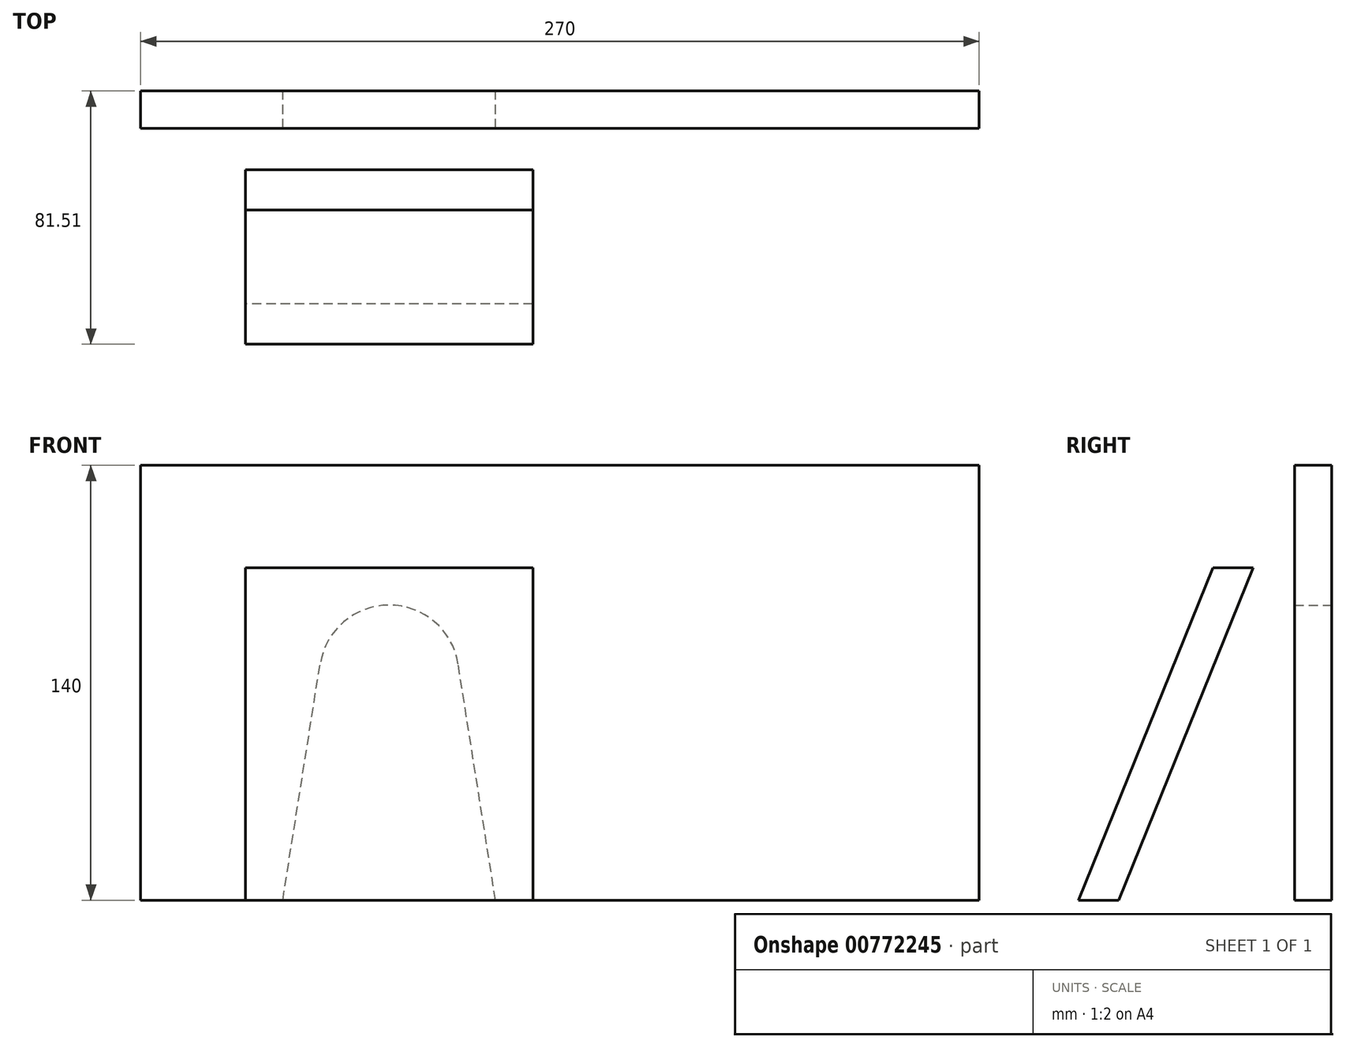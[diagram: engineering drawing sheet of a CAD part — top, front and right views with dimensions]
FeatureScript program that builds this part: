
annotation { "Feature Type Name" : "Feature", "Feature Type Description" : "" }
export const myFeature = defineFeature(function(context is Context, id is Id, definition is map)
    precondition{}
    {
        {
            var Q0;
            Q0=qCreatedBy(makeId("Front.planeOp"),FACE);
            var sketch = newSketch(context, id + "F0", { "sketchPlane" : qUnion([Q0])});
            skLineSegment(sketch, "E0.bottom", {"start": v(0, 0) * mm, "end": v(45.74, 0) * mm});
            skLineSegment(sketch, "E0.top", {"start": v(0, 140) * mm, "end": v(270, 140) * mm});
            skLineSegment(sketch, "E0.left", {"start": v(0, 0) * mm, "end": v(0, 140) * mm});
            skLineSegment(sketch, "E0.right", {"start": v(270, 0) * mm, "end": v(270, 140) * mm});
            skLineSegment(sketch, "E1", {"start": v(80, 140) * mm, "end": v(80, 0) * mm, "construction": true});
            skLineSegment(sketch, "E2", {"start": v(45.74, 0) * mm, "end": v(57.78, 76.02) * mm});
            skLineSegment(sketch, "E3", {"start": v(114.26, 0) * mm, "end": v(102.22, 76.02) * mm});
            skPoint(sketch, "E4", {"position": v(80, 95) * mm});
            skLineSegment(sketch, "E5", {"start": v(102.22, 76.02) * mm, "end": v(102.22, 76.02) * mm});
            skArc(sketch, "E6", {"start": v(102.22, 76.02) * mm, "mid": v(80, 95) * mm, "end": v(57.78, 76.02) * mm});
            skLineSegment(sketch, "E7.trimOffspring", {"start": v(114.26, 0) * mm, "end": v(270, 0) * mm});
            skSolve(sketch);
        }
        {
            var Q0;
            Q0=qSketchRegion(id+"F0",true);
            extrude(context, id + "F1", {"entities" : qUnion([Q0]), "depth" : 12 * mm, "offsetDistance" : 25 * mm});
        }
        {
            var Q0;
            Q0=makeQuery(id+"F1.opExtrude","CAP_FACE",FACE,{"disambiguationData":[OSD([sQuery(id+"F0.wireOp",EDGE,"E0.bottom"),sQuery(id+"F0.wireOp",EDGE,"E0.top"),sQuery(id+"F0.wireOp",EDGE,"E0.left"),sQuery(id+"F0.wireOp",EDGE,"E0.right"),sQuery(id+"F0.wireOp",EDGE,"E2"),sQuery(id+"F0.wireOp",EDGE,"E3"),sQuery(id+"F0.wireOp",EDGE,"E6"),sQuery(id+"F0.wireOp",EDGE,"E7.trimOffspring")])],"isStart":false});
            var sketch = newSketch(context, id + "F2", { "sketchPlane" : qUnion([Q0])});
            skLineSegment(sketch, "E8.0", {"start": v(114.26, 0) * mm, "end": v(114.26, 95) * mm});
            skLineSegment(sketch, "E9", {"start": v(114.26, 0) * mm, "end": v(126.26, 0) * mm});
            skLineSegment(sketch, "E10", {"start": v(126.26, 0) * mm, "end": v(126.26, 95) * mm});
            skLineSegment(sketch, "E11", {"start": v(126.26, 95) * mm, "end": v(114.26, 95) * mm});
            skLineSegment(sketch, "E12", {"start": v(33.74, 0) * mm, "end": v(33.74, 95) * mm});
            skLineSegment(sketch, "E13", {"start": v(33.74, 95) * mm, "end": v(45.74, 95) * mm});
            skLineSegment(sketch, "E14", {"start": v(33.74, 95) * mm, "end": v(126.26, 95) * mm});
            skPoint(sketch, "E14.startSnap0", {"position": v(80, 95) * mm});
            skLineSegment(sketch, "E15", {"start": v(33.74, 107) * mm, "end": v(126.26, 107) * mm});
            skLineSegment(sketch, "E16", {"start": v(33.74, 95) * mm, "end": v(33.74, 107) * mm});
            skLineSegment(sketch, "E17", {"start": v(126.26, 95) * mm, "end": v(126.26, 107) * mm});
            skLineSegment(sketch, "E18", {"start": v(45.74, 0) * mm, "end": v(33.74, 0) * mm});
            skLineSegment(sketch, "E19", {"start": v(45.74, 0) * mm, "end": v(45.74, 95) * mm});
            skSolve(sketch);
        }
        {
            var Q0;
            {var subQ3=sQuery(id+"F2.wireOp",EDGE,"E10");Q0=makeQuery(id+"F2.imprint","IMPRINT",FACE,{"disambiguationData":[TD([[makeQuery(id+"F2.imprint","IMPRINT",EDGE,{"derivedFrom":subQ3}),-1.0]])]});}
            var Q1;
            Q1=makeQuery(id+"F1.opExtrude","CAP_EDGE",EDGE,{"disambiguationData":[OSD([sQuery(id+"F0.wireOp",EDGE,"E0.top")])],"isStart":false});
            cPlane(context, id + "F3", {"entities" : qUnion([Q0, Q1]), "cplaneType" : CPlaneType.LINE_ANGLE, "offset" : 25 * mm, "angle" : 22 * degree, "oppositeDirection" : true, "width" : 150 * mm, "height" : 150 * mm});
        }
        {
            var Q0;
            Q0=qCreatedBy(id+"F3.planeOp",FACE);
            cPlane(context, id + "F4", {"entities" : qUnion([Q0]), "cplaneType" : CPlaneType.OFFSET, "offset" : 12 * mm, "oppositeDirection" : true, "width" : 150 * mm, "height" : 150 * mm});
        }
        {
            var Q0;
            {var subQ4=sQuery(id+"F2.wireOp",EDGE,"E12");Q0=makeQuery(id+"F2.imprint","IMPRINT",FACE,{"disambiguationData":[TD([[makeQuery(id+"F2.imprint","IMPRINT",EDGE,{"derivedFrom":subQ4}),-1.0]])]});}
            var Q1;
            Q1=qCreatedBy(id+"F3.planeOp",FACE);
            extrude(context, id + "F5", {"entities" : qUnion([Q0]), "endBound" : BoundingType.UP_TO_SURFACE, "depth" : 55 * mm, "endBoundEntityFace" : qUnion([Q1]), "offsetDistance" : 25 * mm});
        }
        {
            var Q0;
            {var subQ1=sQuery(id+"F2.wireOp",EDGE,"E9");Q0=makeQuery(id+"F2.imprint","IMPRINT",FACE,{"disambiguationData":[TD([[makeQuery(id+"F2.imprint","IMPRINT",EDGE,{"derivedFrom":subQ1}),1.0]])]});}
            var Q1;
            Q1=qCreatedBy(id+"F3.planeOp",FACE);
            extrude(context, id + "F6", {"entities" : qUnion([Q0]), "endBound" : BoundingType.UP_TO_SURFACE, "depth" : 55 * mm, "endBoundEntityFace" : qUnion([Q1]), "offsetDistance" : 25 * mm});
        }
        {
            var Q0;
            Q0=makeQuery(id+"F2.imprint","IMPRINT",FACE,{"disambiguationData":[TD([[makeQuery(id+"F2.imprint","IMPRINT",EDGE,{"derivedFrom":sQuery(id+"F2.wireOp",EDGE,"E15")}),-1.0]])]});
            var Q1;
            Q1=qCreatedBy(id+"F3.planeOp",FACE);
            extrude(context, id + "F7", {"entities" : qUnion([Q0]), "endBound" : BoundingType.UP_TO_SURFACE, "depth" : 55 * mm, "endBoundEntityFace" : qUnion([Q1]), "offsetDistance" : 25 * mm});
        }
        {
            var Q0;
            {var subQ3=sQuery(id+"F2.wireOp",EDGE,"E10");Q0=makeQuery(id+"F2.imprint","IMPRINT",FACE,{"disambiguationData":[TD([[makeQuery(id+"F2.imprint","IMPRINT",EDGE,{"derivedFrom":subQ3}),-1.0]])]});}
            var sketch = newSketch(context, id + "F8", { "sketchPlane" : qUnion([Q0])});
            skLineSegment(sketch, "E20.0", {"start": v(33.74, 0) * mm, "end": v(33.74, 95) * mm});
            skLineSegment(sketch, "E21.0", {"start": v(33.74, 95) * mm, "end": v(33.74, 107) * mm});
            skLineSegment(sketch, "E22.0", {"start": v(33.74, 107) * mm, "end": v(126.26, 107) * mm});
            skLineSegment(sketch, "E23.0", {"start": v(126.26, 0) * mm, "end": v(126.26, 95) * mm});
            skLineSegment(sketch, "E24", {"start": v(33.74, 0) * mm, "end": v(126.26, 0) * mm});
            skLineSegment(sketch, "E25.0", {"start": v(126.26, 95) * mm, "end": v(126.26, 107) * mm});
            skSolve(sketch);
        }
        {
            var Q0;
            Q0=qSketchRegion(id+"F8",true);
            var Q1;
            Q1=qCreatedBy(id+"F4.planeOp",FACE);
            extrude(context, id + "F9", {"entities" : qUnion([Q0]), "endBound" : BoundingType.UP_TO_SURFACE, "depth" : 25 * mm, "endBoundEntityFace" : qUnion([Q1]), "offsetDistance" : 25 * mm});
        }
        {
            var Q0;
            Q0=qSketchRegion(id+"F8",true);
            var Q1;
            Q1=qCreatedBy(id+"F3.planeOp",FACE);
            extrude(context, id + "F10", {"entities" : qUnion([Q0]), "operationType" : NewBodyOperationType.REMOVE, "endBound" : BoundingType.UP_TO_SURFACE, "depth" : 25 * mm, "endBoundEntityFace" : qUnion([Q1]), "offsetDistance" : 25 * mm});
        }
    });
